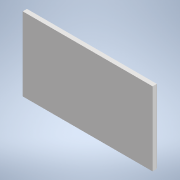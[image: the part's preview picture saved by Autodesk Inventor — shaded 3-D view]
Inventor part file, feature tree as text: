
AUTODESK INVENTOR PART (.ipt)
format: ipt  version: 2020 (Build 240168000, 168)  size: 102,912 bytes
history: native  units: in
note: dims shown in document units (in); Inventor stores cm internally (conversion verified against a paired STEP export)
features: sketch x3, extrude x2, fillet x1
ambient origin geometry x8: Origin, YZ Plane, XZ Plane, XY Plane, X Axis, Y Axis, Z Axis, Center Point
bodies: Solid1 (feature_tree)
feature tree (6):
  extrude  "Extrusion1"  Depth=37.5984in
  fillet  "Fillet1"  Radius=2.4016in
  sketch  "Sketch2"  dims[d4=0.3937in d5=0.1969in d6=0.0in]
  extrude  "Extrusion2"  Depth=0.1969in TaperAngle=0.0deg
  sketch  "Sketch1"  dims[d0=66.2992in d1=37.5984in d2=2.4016in d3=0.0in]
  sketch  "Sketch3"
